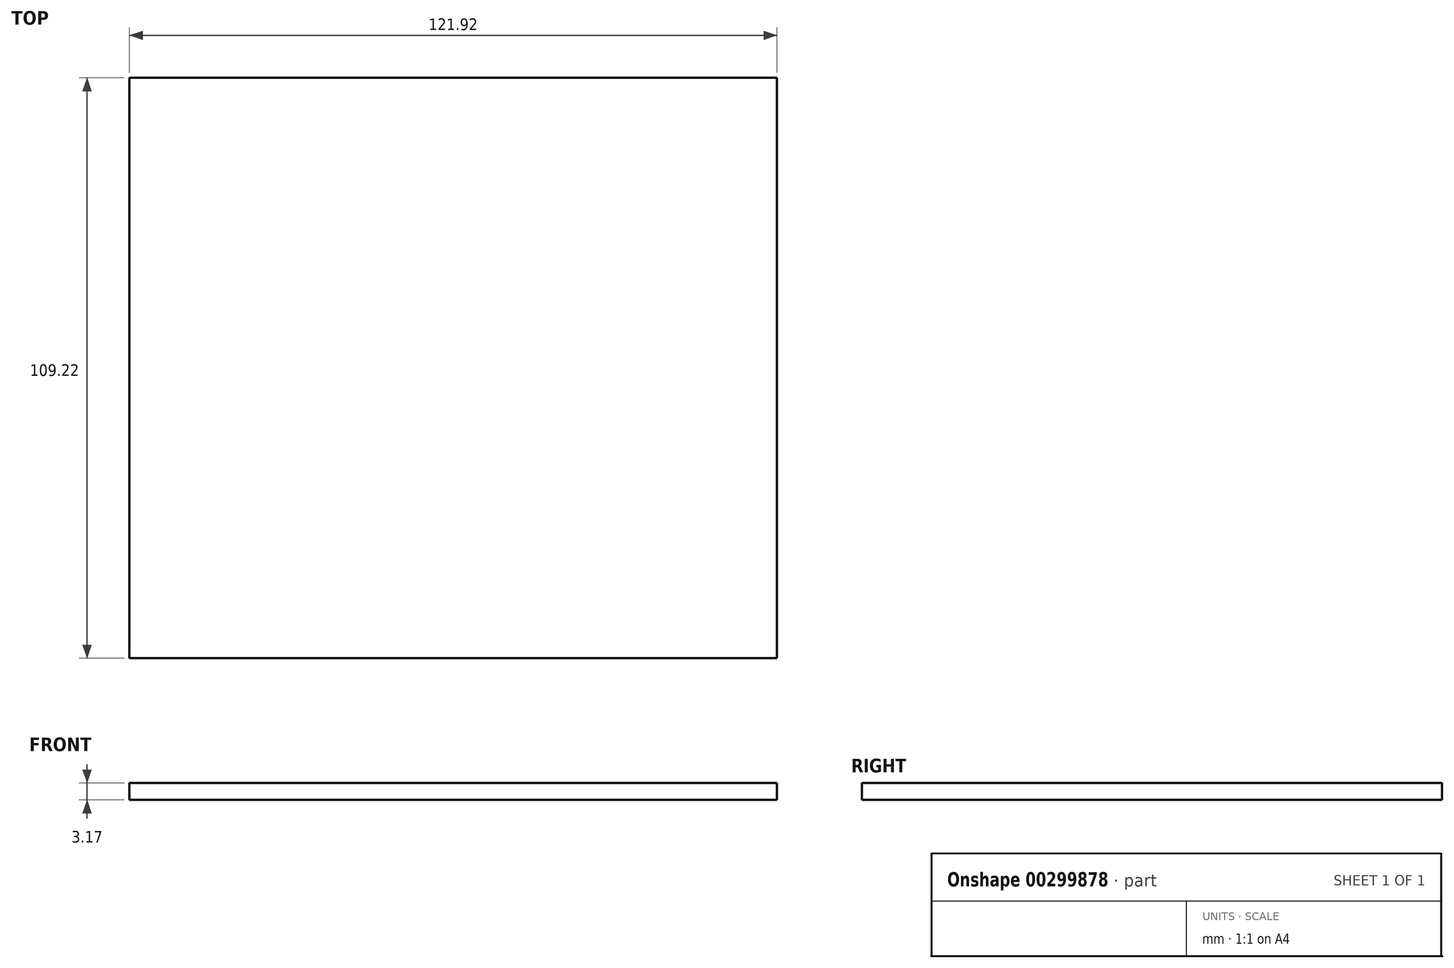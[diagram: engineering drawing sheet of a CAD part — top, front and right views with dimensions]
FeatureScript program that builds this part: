
annotation { "Feature Type Name" : "Feature", "Feature Type Description" : "" }
export const myFeature = defineFeature(function(context is Context, id is Id, definition is map)
    precondition{}
    {
        {
            var Q0;
            Q0=qCreatedBy(makeId("Top.planeOp"),FACE);
            var sketch = newSketch(context, id + "F0", { "sketchPlane" : qUnion([Q0])});
            skLineSegment(sketch, "E0.bottom", {"start": v(-73.66, 67.31) * mm, "end": v(73.66, 67.31) * mm});
            skLineSegment(sketch, "E0.top", {"start": v(-73.66, -67.31) * mm, "end": v(73.66, -67.31) * mm});
            skLineSegment(sketch, "E0.left", {"start": v(-73.66, 67.31) * mm, "end": v(-73.66, -67.31) * mm});
            skLineSegment(sketch, "E0.right", {"start": v(73.66, 67.31) * mm, "end": v(73.66, -67.31) * mm});
            skPoint(sketch, "E0.middle", {"position": v(0, 0) * mm});
            skLineSegment(sketch, "E1.bottom", {"start": v(-73.66, 67.31) * mm, "end": v(48.26, 67.31) * mm});
            skLineSegment(sketch, "E1.top", {"start": v(-73.66, -41.91) * mm, "end": v(48.26, -41.91) * mm});
            skLineSegment(sketch, "E1.left", {"start": v(-73.66, 67.31) * mm, "end": v(-73.66, -41.91) * mm});
            skLineSegment(sketch, "E1.right", {"start": v(48.26, 67.31) * mm, "end": v(48.26, -41.91) * mm});
            skSolve(sketch);
        }
        {
            var Q0;
            Q0=makeQuery(id+"F0.imprint","IMPRINT",FACE,{"disambiguationData":[TD([[makeQuery(id+"F0.imprint","IMPRINT",EDGE,{"derivedFrom":sQuery(id+"F0.wireOp",EDGE,"E0.bottom")}),-1.0]])]});
            extrude(context, id + "F1", {"entities" : qUnion([Q0]), "depth" : 3.17 * mm});
        }
    });
